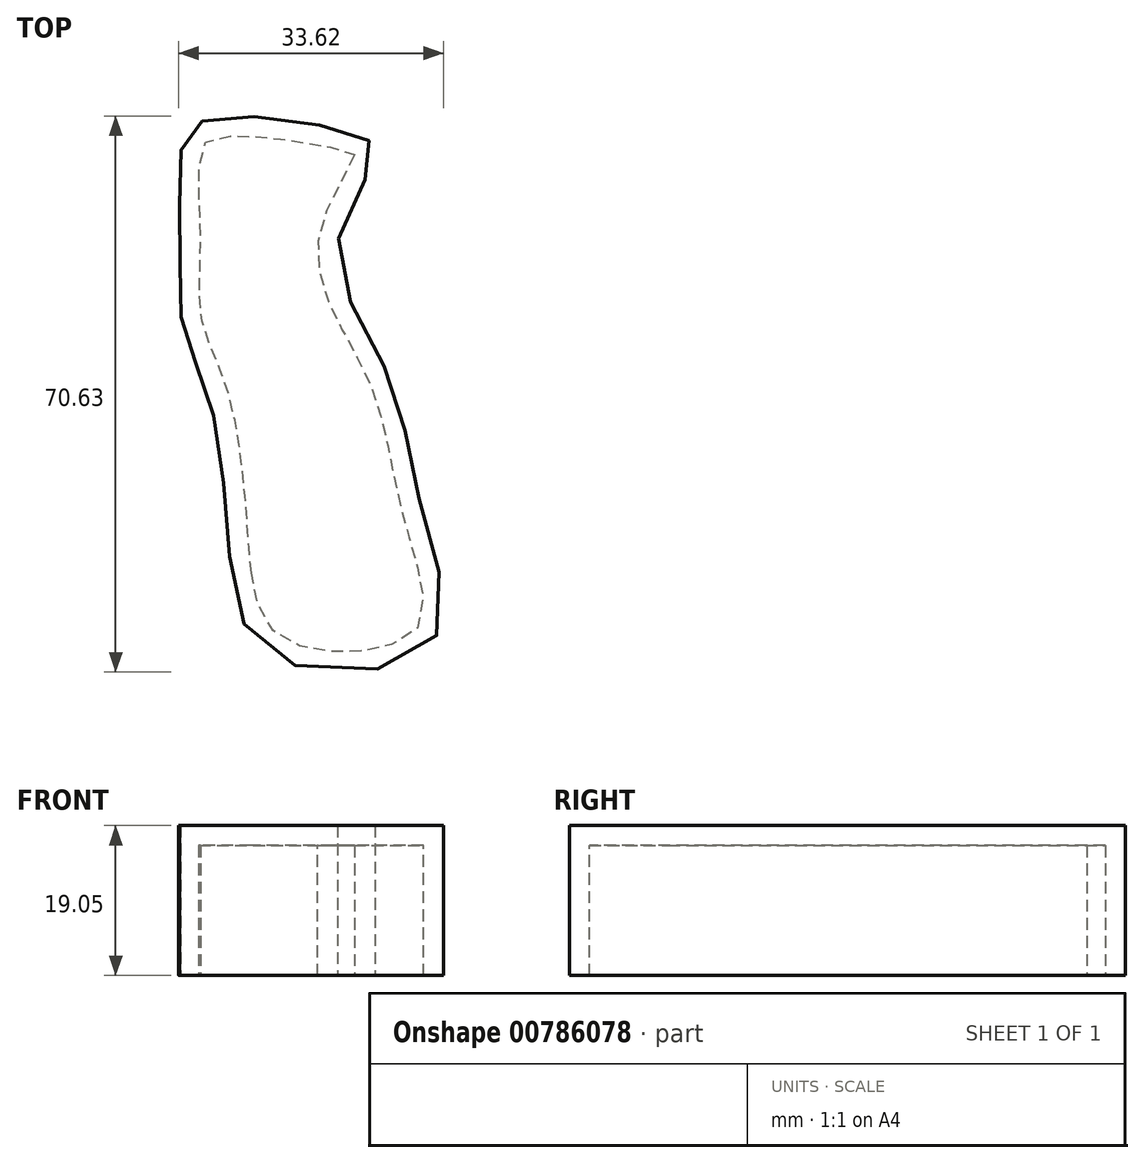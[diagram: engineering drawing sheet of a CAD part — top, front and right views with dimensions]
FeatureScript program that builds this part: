
annotation { "Feature Type Name" : "Feature", "Feature Type Description" : "" }
export const myFeature = defineFeature(function(context is Context, id is Id, definition is map)
    precondition{}
    {
        {
            var Q0;
            Q0=qCreatedBy(makeId("Top.planeOp"),FACE);
            var sketch = newSketch(context, id + "F0", { "sketchPlane" : qUnion([Q0])});
            skFitSpline(sketch, "E0", {"points": [v(20.1, 38.74) * mm, v(27.1, 35.44) * mm, v(22.43, 23.79) * mm, v(28.64, 7.28) * mm, v(33.11, -10.2) * mm, v(34.28, -27.1) * mm, v(14.08, -28.64) * mm, v(8.45, -13.3) * mm, v(5.92, 4.37) * mm, v(2.62, 13.5) * mm, v(2.43, 24.18) * mm, v(2.62, 36.22) * mm, v(6.12, 39.52) * mm, v(20.1, 38.74) * mm]});
            skSolve(sketch);
        }
        {
            var Q0;
            Q0=makeQuery(id+"F0.imprint","IMPRINT",FACE,{"disambiguationData":[TD([[makeQuery(id+"F0.imprint","IMPRINT",EDGE,{"derivedFrom":sQuery(id+"F0.wireOp",EDGE,"E0")}),-1.0]])]});
            extrude(context, id + "F1", {"entities" : qUnion([Q0]), "depth" : 19.05 * mm, "offsetDistance" : 25.4 * mm});
        }
        {
            var Q0;
            Q0=makeQuery(id+"F1.opExtrude","CAP_FACE",FACE,{"disambiguationData":[OSD([sQuery(id+"F0.wireOp",EDGE,"E0")])],"isStart":true});
            shell(context, id + "F2", {"entities" : qUnion([Q0]), "thickness" : 2.54 * mm});
        }
    });
